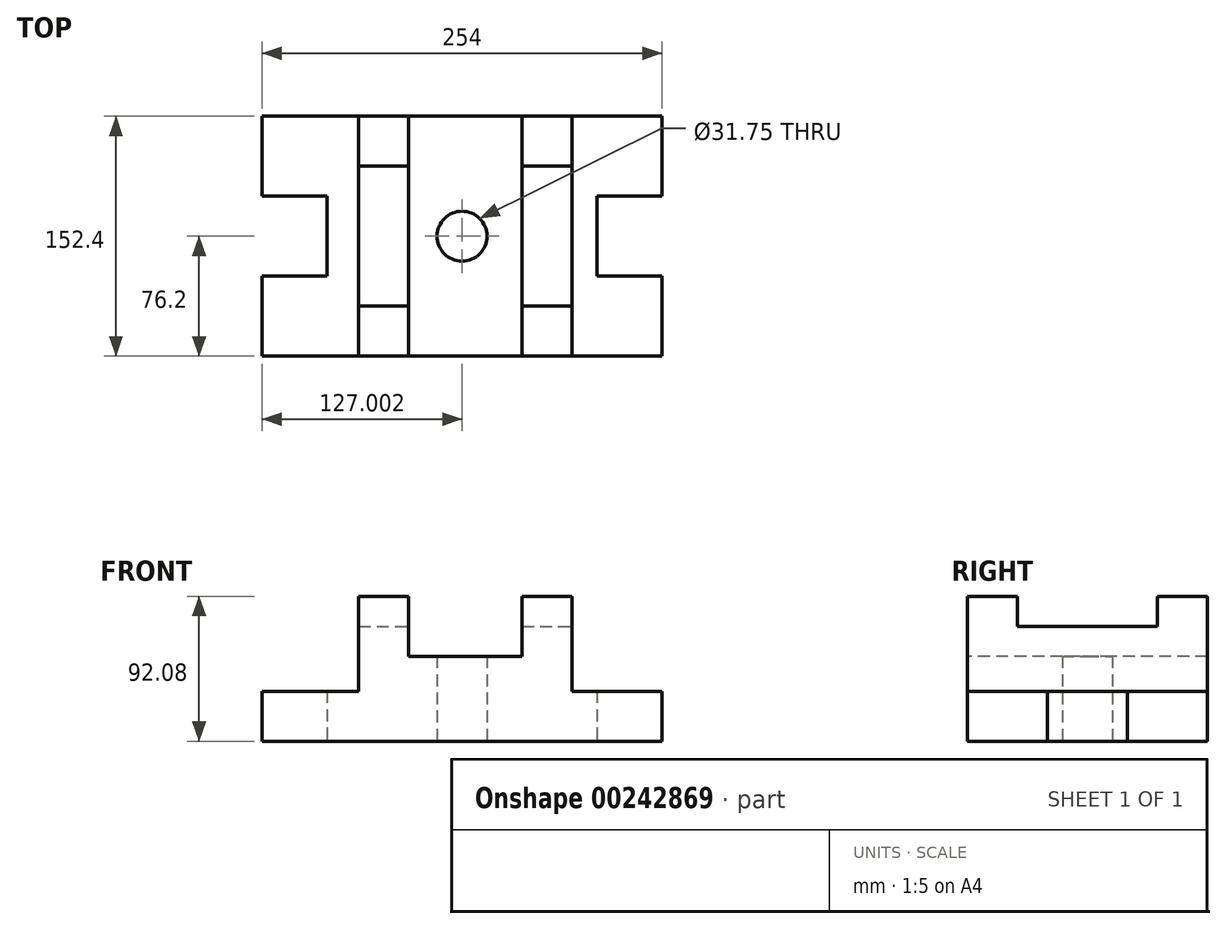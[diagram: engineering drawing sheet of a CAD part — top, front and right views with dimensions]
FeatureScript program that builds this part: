
annotation { "Feature Type Name" : "Feature", "Feature Type Description" : "" }
export const myFeature = defineFeature(function(context is Context, id is Id, definition is map)
    precondition{}
    {
        {
            var Q0;
            Q0=qCreatedBy(makeId("Top.planeOp"),FACE);
            var sketch = newSketch(context, id + "F0", { "sketchPlane" : qUnion([Q0])});
            skLineSegment(sketch, "E0.bottom", {"start": v(-151.12, 76.2) * mm, "end": v(102.88, 76.2) * mm});
            skLineSegment(sketch, "E0.top", {"start": v(-151.12, -76.2) * mm, "end": v(102.88, -76.2) * mm});
            skLineSegment(sketch, "E0.left", {"start": v(-151.12, 76.2) * mm, "end": v(-151.12, 25.4) * mm});
            skLineSegment(sketch, "E0.right", {"start": v(102.88, 76.2) * mm, "end": v(102.88, 25.4) * mm});
            skLineSegment(sketch, "E1.bottom", {"start": v(102.88, 25.4) * mm, "end": v(61.6, 25.4) * mm});
            skLineSegment(sketch, "E1.top", {"start": v(102.88, -25.4) * mm, "end": v(61.6, -25.4) * mm});
            skLineSegment(sketch, "E1.right", {"start": v(61.6, 25.4) * mm, "end": v(61.6, -25.4) * mm});
            skLineSegment(sketch, "E2.bottom", {"start": v(-151.12, 25.4) * mm, "end": v(-109.84, 25.4) * mm});
            skLineSegment(sketch, "E2.top", {"start": v(-151.12, -25.4) * mm, "end": v(-109.84, -25.4) * mm});
            skLineSegment(sketch, "E2.right", {"start": v(-109.84, 25.4) * mm, "end": v(-109.84, -25.4) * mm});
            skLineSegment(sketch, "E3.trimOffspring", {"start": v(-151.12, -25.4) * mm, "end": v(-151.12, -76.2) * mm});
            skLineSegment(sketch, "E4.trimOffspring", {"start": v(102.88, -25.4) * mm, "end": v(102.88, -76.2) * mm});
            skLineSegment(sketch, "E5", {"start": v(13.98, 76.2) * mm, "end": v(13.98, -76.2) * mm});
            skLineSegment(sketch, "E6", {"start": v(45.73, 76.2) * mm, "end": v(45.73, -76.2) * mm});
            skLineSegment(sketch, "E7", {"start": v(13.98, 44.45) * mm, "end": v(45.73, 44.45) * mm});
            skLineSegment(sketch, "E8", {"start": v(13.98, -44.45) * mm, "end": v(45.73, -44.45) * mm});
            skCircle(sketch, "E9", {"center": v(-24.12, 0) * mm, "radius": 15.88 * mm});
            skPoint(sketch, "E9.centerSnap0", {"position": v(-24.12, 76.2) * mm});
            skLineSegment(sketch, "E10", {"start": v(-89.7, 76.2) * mm, "end": v(-89.7, -76.2) * mm});
            skLineSegment(sketch, "E11", {"start": v(-57.96, 76.2) * mm, "end": v(-57.96, -76.2) * mm});
            skLineSegment(sketch, "E12", {"start": v(-89.7, 44.45) * mm, "end": v(-57.96, 44.45) * mm});
            skLineSegment(sketch, "E13", {"start": v(-89.7, -44.45) * mm, "end": v(-57.96, -44.45) * mm});
            skSolve(sketch);
        }
        {
            var Q0;
            {var subQ4=sQuery(id+"F0.wireOp",EDGE,"E0.left");Q0=makeQuery(id+"F0.imprint","IMPRINT",FACE,{"disambiguationData":[TD([[makeQuery(id+"F0.imprint","IMPRINT",EDGE,{"derivedFrom":subQ4}),1.0]])]});}
            var Q1;
            {var subQ0=sQuery(id+"F0.wireOp",EDGE,"E0.right");Q1=makeQuery(id+"F0.imprint","IMPRINT",FACE,{"disambiguationData":[TD([[makeQuery(id+"F0.imprint","IMPRINT",EDGE,{"derivedFrom":subQ0}),-1.0]])]});}
            extrude(context, id + "F1", {"entities" : qUnion([Q0, Q1]), "depth" : 31.75 * mm});
        }
        {
            var Q0;
            Q0=makeQuery(id+"F0.imprint","IMPRINT",FACE,{"disambiguationData":[TD([[makeQuery(id+"F0.imprint","IMPRINT",EDGE,{"derivedFrom":sQuery(id+"F0.wireOp",EDGE,"E9")}),-1.0]])]});
            extrude(context, id + "F2", {"entities" : qUnion([Q0]), "operationType" : NewBodyOperationType.ADD, "depth" : 53.97 * mm});
        }
        {
            var Q0;
            {var subQ5=sQuery(id+"F0.wireOp",EDGE,"E12");Q0=makeQuery(id+"F0.imprint","IMPRINT",FACE,{"disambiguationData":[TD([[makeQuery(id+"F0.imprint","IMPRINT",EDGE,{"derivedFrom":subQ5}),1.0]])]});}
            var Q1;
            {var subQ5=sQuery(id+"F0.wireOp",EDGE,"E13");Q1=makeQuery(id+"F0.imprint","IMPRINT",FACE,{"disambiguationData":[TD([[makeQuery(id+"F0.imprint","IMPRINT",EDGE,{"derivedFrom":subQ5}),-1.0]])]});}
            var Q2;
            {var subQ5=sQuery(id+"F0.wireOp",EDGE,"E8");Q2=makeQuery(id+"F0.imprint","IMPRINT",FACE,{"disambiguationData":[TD([[makeQuery(id+"F0.imprint","IMPRINT",EDGE,{"derivedFrom":subQ5}),-1.0]])]});}
            var Q3;
            {var subQ5=sQuery(id+"F0.wireOp",EDGE,"E7");Q3=makeQuery(id+"F0.imprint","IMPRINT",FACE,{"disambiguationData":[TD([[makeQuery(id+"F0.imprint","IMPRINT",EDGE,{"derivedFrom":subQ5}),1.0]])]});}
            extrude(context, id + "F3", {"entities" : qUnion([Q0, Q1, Q2, Q3]), "operationType" : NewBodyOperationType.ADD, "depth" : 92.07 * mm});
        }
        {
            var Q0;
            {var subQ0=sQuery(id+"F0.wireOp",EDGE,"E12");Q0=makeQuery(id+"F0.imprint","IMPRINT",FACE,{"disambiguationData":[TD([[makeQuery(id+"F0.imprint","IMPRINT",EDGE,{"derivedFrom":subQ0}),-1.0]])]});}
            var Q1;
            {var subQ0=sQuery(id+"F0.wireOp",EDGE,"E7");Q1=makeQuery(id+"F0.imprint","IMPRINT",FACE,{"disambiguationData":[TD([[makeQuery(id+"F0.imprint","IMPRINT",EDGE,{"derivedFrom":subQ0}),-1.0]])]});}
            extrude(context, id + "F4", {"entities" : qUnion([Q0, Q1]), "operationType" : NewBodyOperationType.ADD, "depth" : 73.02 * mm});
        }
    });
